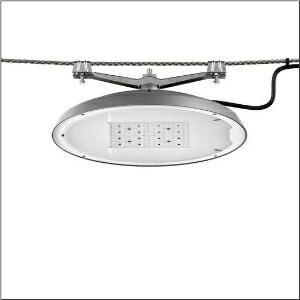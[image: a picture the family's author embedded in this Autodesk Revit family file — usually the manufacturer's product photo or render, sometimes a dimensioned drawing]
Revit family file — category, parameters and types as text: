
# Revit family: dl_r__50_iq_mini___st0_8s_5xa248v31f08me_3f47
name_source: partatom
category: Lighting Fixtures
units: mm (PartAtom-declared; Revit-internal decimal feet)

## family parameters
Cut with Voids When Loaded = No
Host = Face
Light Source = No
Part Type = Normal
Room Calculation Point = No
Round Connector Dimension = Use Diameter
Shared = No

## types (1)
- --- (1 x LED, 15660 lm, 107.8 W, 3000K)
    Apparent Load = 108 VA
    CIE Flux Codes = 38 75 97 100 100
    Color Rendering = 70
    Color Temperature = 3000K
    Default Elevation = 1800 mm
    Description = DL® 50 iQ mini, catenary luminaire, primary light control with lens, of PMMA, primary optical cover: cover, of toughened safety glass, transparent, light distribution: ST0.8s, light emission: direct distribution, primary light characteristic: symmetric, installation type: suspended mounting, LED, High Power LED, rated luminous flux: 15.660lm, luminous efficacy: 145lm/W, light colour: 730, colour temperature: 3000K, control gear: iQ Street-Remote, control: optimised constant luminous flux control (CLO 2.0), Desk-Remote (wireless, voltage-free reading and setting of iQ features in the workshop via application-optimized NFC function/RFID function), Light-Fading, Smart-Wire, Night-Set, Lumen-Switch, Temp-Guard, Auto-Match, Street-Remote, mains connection: 230..240V, AC, 50/60Hz, start of lifetime: 108W, end of service life: 118W, reduction: 47W, luminaire housing, of diecast aluminium, powder-coated, Siteco® metallic grey (DB 702S), diameter: 500mm, height: 115mm, mounting height: 4..12m, protection rating (complete): IP66, insulation class (complete): insulation class II (safety insulation), certification: CE, ENEC, ENEC+, VDE, impact resistance: IK08, permissible operating ambient temperature for outdoor applications: -25..+40°C, standard-compliant lighting for roads and squares, packaging unit: 1 piece

Light Distribution: ST0.8s
    Height = 124 mm  [stored 0.406824 ft]
    Lamp = 1 x LED
    Lamp Light Flux = 15660 lm
    Lamp Power = 107.8 W
    Lamp count = 1
    Length = 500 mm
    Luminous efficacy = 145 lm/W
    Manufacturer = Siteco
    ModVariant = No
    Model = 5XA248V31F08ME
    Number of Poles = 1
    OnlyDefault = Yes
    Power Factor = 1
    Product Name = DL® 50 iQ mini | ST0.8s
    Product group = catenary luminaire
    ProductGroupID = 6300
    Protection Class = Protection class II
    Protection Degree = IP 66
    RLX_Detail_Level = 1
    RLX_Emergency_Light_Flux = 0 lm
    RLX_Emergency_Type = 0
    RLX_Emergency_Type_DB = No
    RlxData = <blob elided: 126829 chars, md5=14a35948>
    Socket = socket
    Standby Power = 0 W
    System Light Flux = 15660 lm
    System Power = 108 W
    Type Comments = factory setting: luminous flux: 100 % | dim-lin: 254 | 565 mA
    Type Image = l_1251783.jpg
    URL = http://relux.com
    VarID = @adj_140982
    Voltage = 0 V
    Weight = 0.00 kg
    Width = 0 mm  [stored 0 ft]

note: [stored X ft] marks values corroborated as IEEE doubles in the binary element streams (Revit-internal decimal feet)

## geometry (parser evidence)
native form markers: Blend x4, Sweep x13
no freeform markers — native parametric forms only
